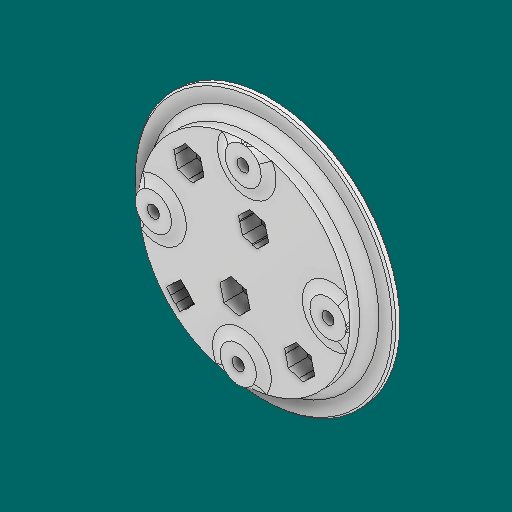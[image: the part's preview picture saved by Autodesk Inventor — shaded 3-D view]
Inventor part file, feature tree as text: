
AUTODESK INVENTOR PART (.ipt)
format: ipt  version: 2023.1 (Build 271208000, 208)  size: 652,800 bytes
history: native  units: in
note: dims shown in document units (in); Inventor stores cm internally (conversion verified against a paired STEP export)
features: sketch x6, other x3
ambient origin geometry x8: Origin, YZ Plane, XZ Plane, XY Plane, X Axis, Y Axis, Z Axis, Center Point
bodies: Solid1 (feature_tree)
feature tree (9):
  other  "SteeringCoupler.ipt"
  other  "Solid1::SteeringCoupler.ipt"
  other  "TaggingFeature1"
  sketch  "Sketch1"  dims[d0=0.3937in]
  sketch  "Sketch2"
  sketch  "Sketch4"
  sketch  "Sketch5"
  sketch  "Sketch6"
  sketch  "Sketch8"
